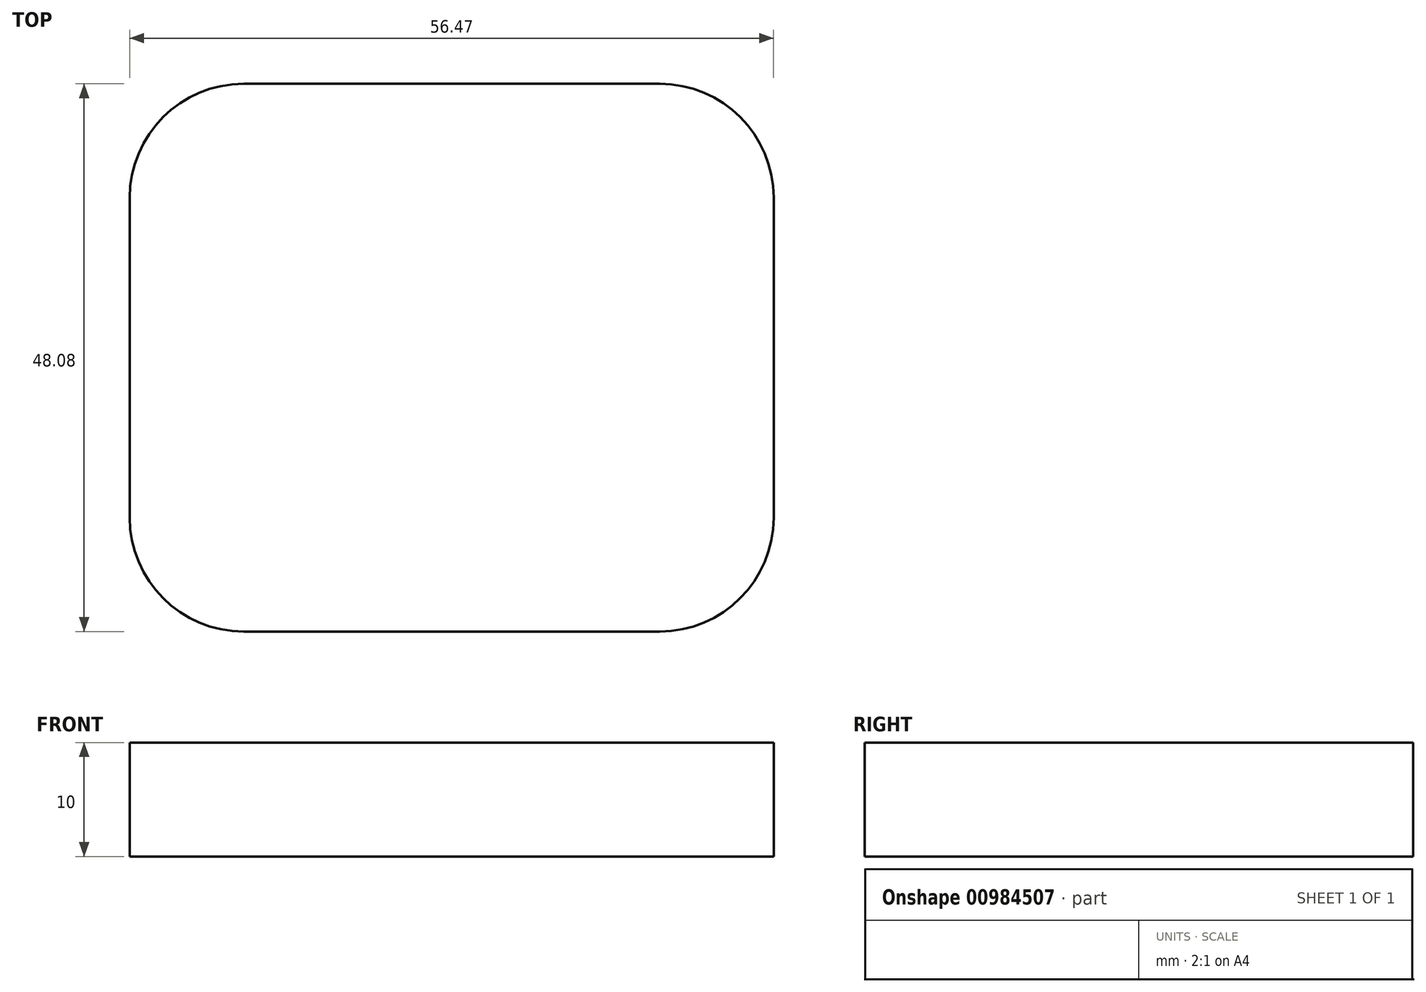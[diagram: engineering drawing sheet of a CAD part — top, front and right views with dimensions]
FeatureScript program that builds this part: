
annotation { "Feature Type Name" : "Feature", "Feature Type Description" : "" }
export const myFeature = defineFeature(function(context is Context, id is Id, definition is map)
    precondition{}
    {
        {
            var Q0;
            Q0=qCreatedBy(makeId("Top.planeOp"),FACE);
            var sketch = newSketch(context, id + "F0", { "sketchPlane" : qUnion([Q0])});
            skLineSegment(sketch, "E0", {"start": v(0, 0) * mm, "end": v(56.47, 0) * mm});
            skLineSegment(sketch, "E1", {"start": v(0, 0) * mm, "end": v(0, -48.08) * mm});
            skLineSegment(sketch, "E2", {"start": v(0, -48.08) * mm, "end": v(56.47, -48.08) * mm});
            skLineSegment(sketch, "E3", {"start": v(56.47, 0) * mm, "end": v(56.47, -48.08) * mm});
            skSolve(sketch);
        }
        {
            var Q0;
            Q0 = qSketchRegion(id + "F0", false);
            extrude(context, id + "F1", {"entities" : qUnion([Q0]), "depth" : 10 * mm});
        }
        {
            var Q0;
            {var subQ0=sQuery(id+"F0.wireOp",EDGE,"E3");var subQ1=sQuery(id+"F0.wireOp",EDGE,"E2");var subQ2=sQuery(id+"F0.wireOp",EDGE,"E1");var subQ3=sQuery(id+"F0.wireOp",EDGE,"E0");Q0=qUnion([makeQuery(id+"F1.opExtrude","SWEPT_EDGE",EDGE,{"disambiguationData":[OSD([subQ3,subQ0])]}),makeQuery(id+"F1.opExtrude","SWEPT_EDGE",EDGE,{"disambiguationData":[OSD([subQ3,subQ2])]}),makeQuery(id+"F1.opExtrude","SWEPT_EDGE",EDGE,{"disambiguationData":[OSD([subQ2,subQ1])]}),makeQuery(id+"F1.opExtrude","SWEPT_EDGE",EDGE,{"disambiguationData":[OSD([subQ1,subQ0])]})]);}
            fillet(context, id + "F2", {"entities" : qUnion([Q0]), "radius" : 10 * mm, "tangentPropagation" : true, "allowEdgeOverflow" : false});
        }
        {
            var Q0;
            Q0=qCreatedBy(makeId("Top.planeOp"),FACE);
            var sketch = newSketch(context, id + "F3", { "sketchPlane" : qUnion([Q0])});
            skLineSegment(sketch, "E4", {"start": v(0, 0) * mm, "end": v(56.47, 0) * mm});
            skLineSegment(sketch, "E5", {"start": v(0, 0) * mm, "end": v(0, -48.08) * mm});
            skLineSegment(sketch, "E6", {"start": v(0, -48.08) * mm, "end": v(56.47, -48.08) * mm});
            skLineSegment(sketch, "E7", {"start": v(56.47, 0) * mm, "end": v(56.47, -48.08) * mm});
            skSolve(sketch);
        }
        {
            var Q0;
            Q0 = qSketchRegion(id + "F3", false);
            extrude(context, id + "F4", {"entities" : qUnion([Q0]), "depth" : 10 * mm});
        }
        {
            var Q0;
            {var subQ0=sQuery(id+"F3.wireOp",EDGE,"E7");var subQ1=sQuery(id+"F3.wireOp",EDGE,"E6");var subQ2=sQuery(id+"F3.wireOp",EDGE,"E5");var subQ3=sQuery(id+"F3.wireOp",EDGE,"E4");Q0=qUnion([makeQuery(id+"F4.opExtrude","SWEPT_EDGE",EDGE,{"disambiguationData":[OSD([subQ3,subQ0])]}),makeQuery(id+"F4.opExtrude","SWEPT_EDGE",EDGE,{"disambiguationData":[OSD([subQ3,subQ2])]}),makeQuery(id+"F4.opExtrude","SWEPT_EDGE",EDGE,{"disambiguationData":[OSD([subQ2,subQ1])]}),makeQuery(id+"F4.opExtrude","SWEPT_EDGE",EDGE,{"disambiguationData":[OSD([subQ1,subQ0])]})]);}
            fillet(context, id + "F5", {"entities" : qUnion([Q0]), "radius" : 10 * mm, "tangentPropagation" : true, "allowEdgeOverflow" : false});
        }
    });
